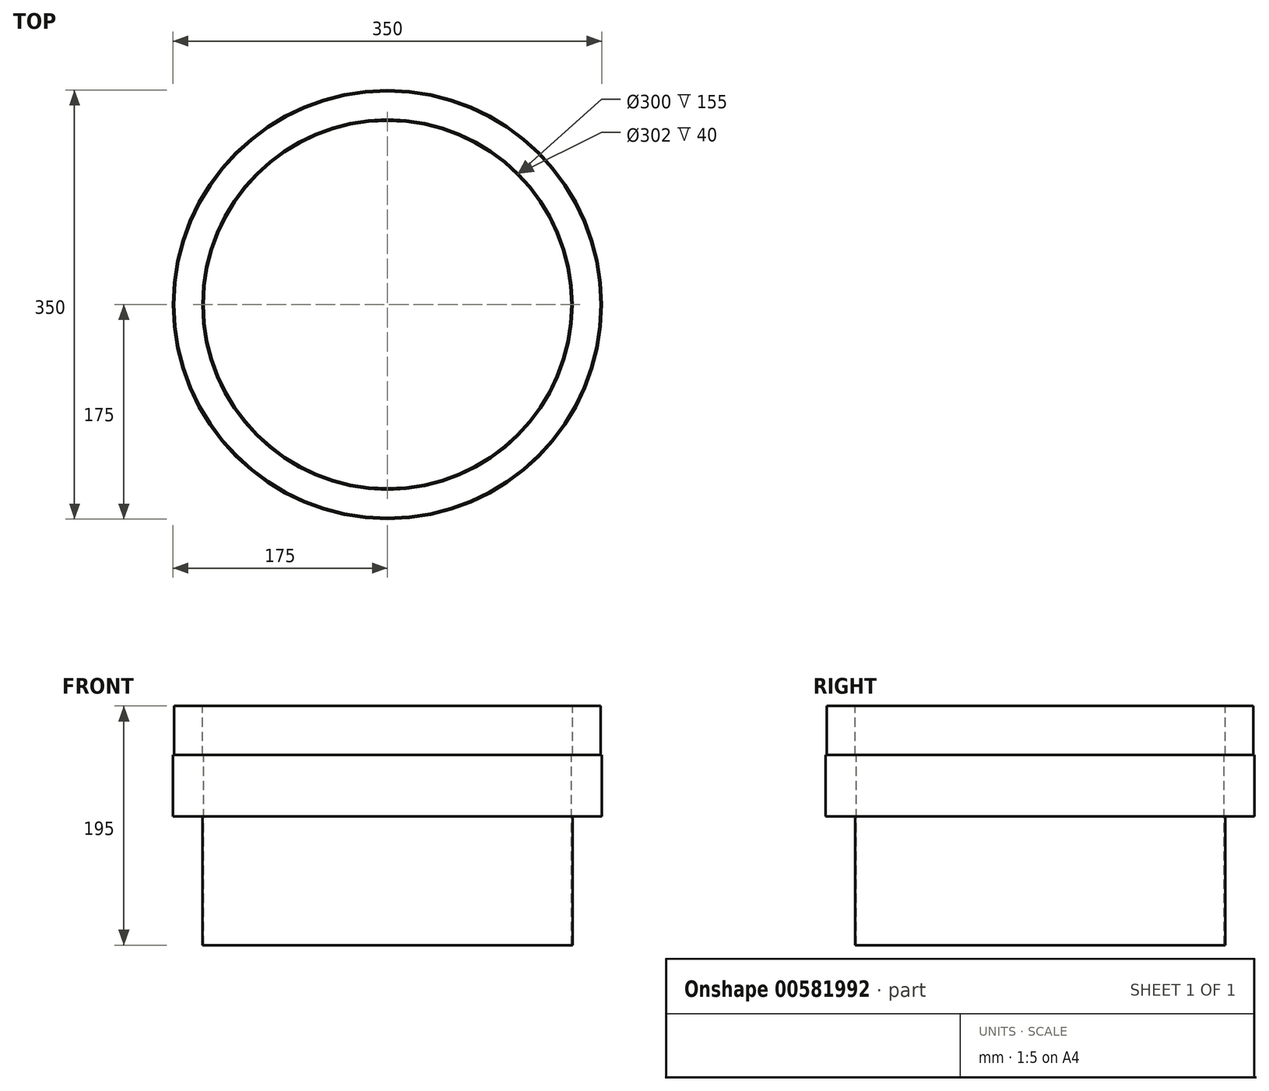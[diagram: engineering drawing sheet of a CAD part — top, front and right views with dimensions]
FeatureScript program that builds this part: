
annotation { "Feature Type Name" : "Feature", "Feature Type Description" : "" }
export const myFeature = defineFeature(function(context is Context, id is Id, definition is map)
    precondition{}
    {
        {
            var Q0;
            Q0=qCreatedBy(makeId("Front.planeOp"),FACE);
            var sketch = newSketch(context, id + "F0", { "sketchPlane" : qUnion([Q0])});
            skLineSegment(sketch, "E0", {"start": v(0, 710.75) * mm, "end": v(0, -704.58) * mm, "construction": true});
            skLineSegment(sketch, "E1", {"start": v(-150, 295.65) * mm, "end": v(-150, 410.65) * mm});
            skLineSegment(sketch, "E2", {"start": v(-150, 410.65) * mm, "end": v(-151, 410.65) * mm});
            skLineSegment(sketch, "E3", {"start": v(-174, 410.65) * mm, "end": v(-175, 410.65) * mm});
            skLineSegment(sketch, "E4", {"start": v(-175, 410.65) * mm, "end": v(-175, 360.65) * mm});
            skLineSegment(sketch, "E5", {"start": v(-175, 360.65) * mm, "end": v(-151, 360.65) * mm});
            skLineSegment(sketch, "E6", {"start": v(-151, 360.65) * mm, "end": v(-151, 295.65) * mm});
            skLineSegment(sketch, "E7", {"start": v(-174, 450.65) * mm, "end": v(-174, 410.65) * mm});
            skLineSegment(sketch, "E8", {"start": v(-174, 450.65) * mm, "end": v(-151, 450.65) * mm});
            skLineSegment(sketch, "E9", {"start": v(-151, 410.65) * mm, "end": v(-151, 450.65) * mm});
            skLineSegment(sketch, "E10", {"start": v(-150, 295.65) * mm, "end": v(-150, 255.65) * mm});
            skLineSegment(sketch, "E11", {"start": v(-151, 295.65) * mm, "end": v(-151, 255.65) * mm});
            skLineSegment(sketch, "E12", {"start": v(-151, 255.65) * mm, "end": v(-150, 255.65) * mm});
            skSolve(sketch);
        }
        {
            var Q0;
            Q0=qSketchRegion(id+"F0",true);
            var Q1;
            Q1=sQuery(id+"F0.wireOp",EDGE,"E0");
            revolve(context, id + "F1", {"entities" : qUnion([Q0]), "axis" : qUnion([Q1]), "revolveType" : RevolveType.FULL});
        }
    });
